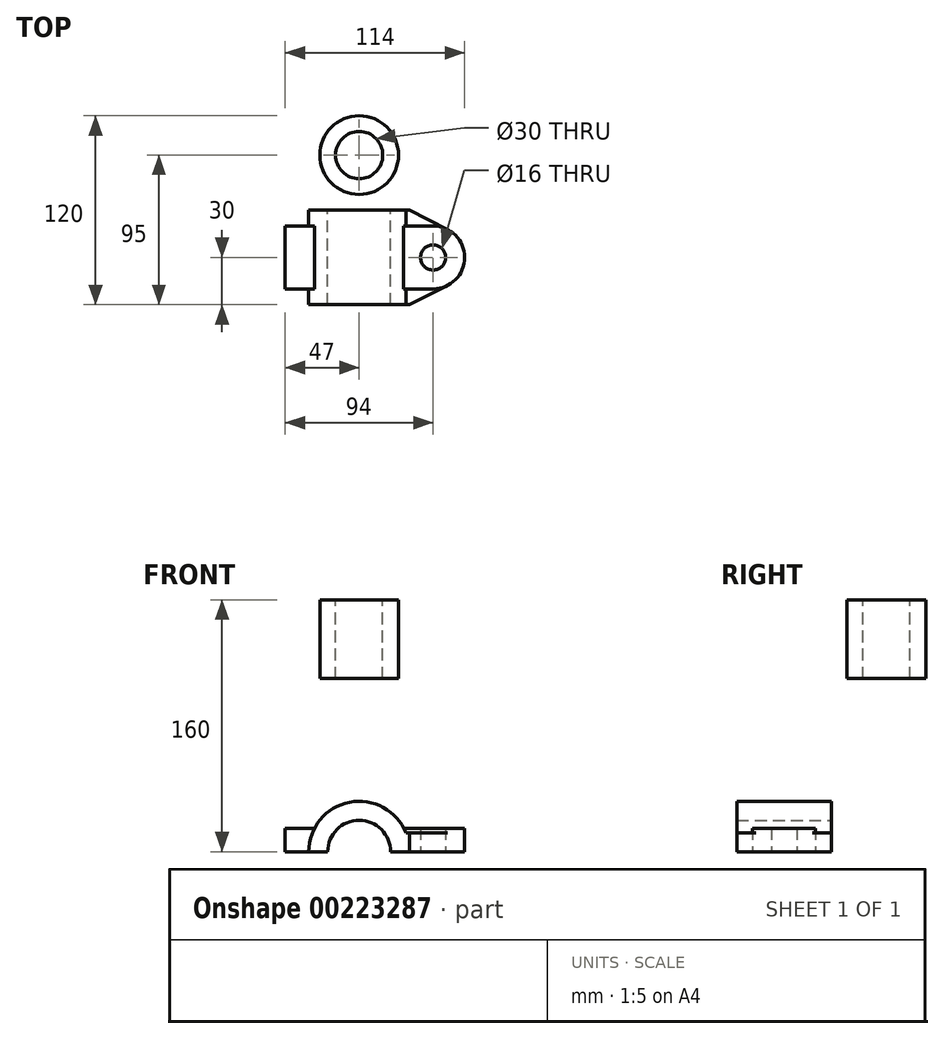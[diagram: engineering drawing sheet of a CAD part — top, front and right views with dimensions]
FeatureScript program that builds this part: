
annotation { "Feature Type Name" : "Feature", "Feature Type Description" : "" }
export const myFeature = defineFeature(function(context is Context, id is Id, definition is map)
    precondition{}
    {
        {
            var Q0;
            Q0=qCreatedBy(makeId("Front.planeOp"),FACE);
            var sketch = newSketch(context, id + "F0", { "sketchPlane" : qUnion([Q0])});
            skArc(sketch, "E0", {"start": v(32, 0) * mm, "mid": v(0, 32) * mm, "end": v(-32, 0) * mm});
            skArc(sketch, "E1", {"start": v(20, 0) * mm, "mid": v(0, 20) * mm, "end": v(-20, 0) * mm});
            skLineSegment(sketch, "E2", {"start": v(-47, 0) * mm, "end": v(47, 0) * mm});
            skLineSegment(sketch, "E3", {"start": v(47, 0) * mm, "end": v(47, 15) * mm});
            skLineSegment(sketch, "E4", {"start": v(47, 15) * mm, "end": v(28.27, 15) * mm});
            skLineSegment(sketch, "E5", {"start": v(-47, 15) * mm, "end": v(-47, 0) * mm});
            skLineSegment(sketch, "E6", {"start": v(0, 67.2) * mm, "end": v(0, -78.93) * mm, "construction": true});
            skLineSegment(sketch, "E7.trimOffspring", {"start": v(-28.27, 15) * mm, "end": v(-47, 15) * mm});
            skSolve(sketch);
        }
        {
            var Q0;
            {var subQ0=sQuery(id+"F0.wireOp",EDGE,"E1");Q0=makeQuery(id+"F0.imprint","IMPRINT",FACE,{"disambiguationData":[TD([[makeQuery(id+"F0.imprint","IMPRINT",EDGE,{"derivedFrom":subQ0}),-1.0]])]});}
            extrude(context, id + "F1", {"entities" : qUnion([Q0]), "endBound" : BoundingType.SYMMETRIC, "depth" : 60 * mm});
        }
        {
            var Q0;
            {var subQ4=sQuery(id+"F0.wireOp",EDGE,"E5");Q0=makeQuery(id+"F0.imprint","IMPRINT",FACE,{"disambiguationData":[TD([[makeQuery(id+"F0.imprint","IMPRINT",EDGE,{"derivedFrom":subQ4}),1.0]])]});}
            var Q1;
            {var subQ4=sQuery(id+"F0.wireOp",EDGE,"E3");Q1=makeQuery(id+"F0.imprint","IMPRINT",FACE,{"disambiguationData":[TD([[makeQuery(id+"F0.imprint","IMPRINT",EDGE,{"derivedFrom":subQ4}),1.0]])]});}
            extrude(context, id + "F2", {"entities" : qUnion([Q0, Q1]), "operationType" : NewBodyOperationType.ADD, "endBound" : BoundingType.SYMMETRIC, "depth" : 40 * mm});
        }
        {
            var Q0;
            Q0=qCreatedBy(makeId("Top.planeOp"),FACE);
            var sketch = newSketch(context, id + "F3", { "sketchPlane" : qUnion([Q0])});
            skCircle(sketch, "E8", {"center": v(47, 0) * mm, "radius": 8 * mm});
            skCircle(sketch, "E9", {"center": v(47, 0) * mm, "radius": 20 * mm});
            skLineSegment(sketch, "E10.0", {"start": v(32, -20) * mm, "end": v(28.27, -20) * mm});
            skLineSegment(sketch, "E11.0", {"start": v(32, 20) * mm, "end": v(28.27, 20) * mm});
            skLineSegment(sketch, "E12", {"start": v(32, -30) * mm, "end": v(56.03, -17.85) * mm});
            skLineSegment(sketch, "E13", {"start": v(32, 30) * mm, "end": v(56.03, 17.85) * mm});
            skPoint(sketch, "E14.0.start.orphan", {"position": v(32, 20) * mm});
            skPoint(sketch, "E15.0.end.orphan", {"position": v(32, -20) * mm});
            skLineSegment(sketch, "E16", {"start": v(32, -30) * mm, "end": v(22, -30) * mm});
            skLineSegment(sketch, "E17", {"start": v(22, -30) * mm, "end": v(22, -20) * mm});
            skLineSegment(sketch, "E18", {"start": v(22, -20) * mm, "end": v(47, -20) * mm});
            skLineSegment(sketch, "E19", {"start": v(47, 20) * mm, "end": v(22, 20) * mm});
            skLineSegment(sketch, "E20", {"start": v(22, 20) * mm, "end": v(22, 30) * mm});
            skLineSegment(sketch, "E21", {"start": v(22, 30) * mm, "end": v(32, 30) * mm});
            skSolve(sketch);
        }
        {
            var Q0;
            Q0=makeQuery(id+"F3.imprint","IMPRINT",FACE,{"disambiguationData":[TD([[makeQuery(id+"F3.imprint","IMPRINT",EDGE,{"derivedFrom":sQuery(id+"F3.wireOp",EDGE,"E8")}),-1.0]])]});
            extrude(context, id + "F4", {"entities" : qUnion([Q0]), "operationType" : NewBodyOperationType.ADD, "depth" : 15 * mm});
        }
        {
            var Q0;
            {var subQ4=sQuery(id+"F3.wireOp",EDGE,"E13");Q0=makeQuery(id+"F3.imprint","IMPRINT",FACE,{"disambiguationData":[TD([[makeQuery(id+"F3.imprint","IMPRINT",EDGE,{"derivedFrom":subQ4}),-1.0]])]});}
            var Q1;
            {var subQ1=sQuery(id+"F3.wireOp",EDGE,"E12");Q1=makeQuery(id+"F3.imprint","IMPRINT",FACE,{"disambiguationData":[TD([[makeQuery(id+"F3.imprint","IMPRINT",EDGE,{"derivedFrom":subQ1}),1.0]])]});}
            extrude(context, id + "F5", {"entities" : qUnion([Q0, Q1]), "operationType" : NewBodyOperationType.ADD, "depth" : 12 * mm});
        }
        {
            var Q0;
            Q0=makeQuery(id+"F3.imprint","IMPRINT",FACE,{"disambiguationData":[TD([[makeQuery(id+"F3.imprint","IMPRINT",EDGE,{"derivedFrom":sQuery(id+"F3.wireOp",EDGE,"E8")}),1.0]])]});
            extrude(context, id + "F6", {"entities" : qUnion([Q0]), "operationType" : NewBodyOperationType.REMOVE, "depth" : 25 * mm});
        }
        {
            var Q0;
            Q0=qCreatedBy(makeId("Top.planeOp"),FACE);
            cPlane(context, id + "F7", {"entities" : qUnion([Q0]), "cplaneType" : CPlaneType.OFFSET, "offset" : 160 * mm, "width" : 150 * mm, "height" : 150 * mm});
        }
        {
            var Q0;
            Q0=qCreatedBy(id+"F7.planeOp",FACE);
            var sketch = newSketch(context, id + "F8", { "sketchPlane" : qUnion([Q0])});
            skCircle(sketch, "E22", {"center": v(0, 65) * mm, "radius": 25 * mm});
            skCircle(sketch, "E23", {"center": v(0, 65) * mm, "radius": 15 * mm});
            skLineSegment(sketch, "E24", {"start": v(0, -98.9) * mm, "end": v(0, 161.69) * mm, "construction": true});
            skLineSegment(sketch, "E25", {"start": v(-5, 65) * mm, "end": v(5, 65) * mm});
            skLineSegment(sketch, "E26", {"start": v(5, -46.71) * mm, "end": v(-5, -46.71) * mm});
            skLineSegment(sketch, "E27.0", {"start": v(29.66, -30) * mm, "end": v(-29.66, -30) * mm, "construction": true});
            skSolve(sketch);
        }
        {
            var Q0;
            Q0=makeQuery(id+"F8.imprint","IMPRINT",FACE,{"disambiguationData":[TD([[makeQuery(id+"F8.imprint","IMPRINT",EDGE,{"derivedFrom":sQuery(id+"F8.wireOp",EDGE,"E22")}),1.0]])]});
            extrude(context, id + "F9", {"entities" : qUnion([Q0]), "oppositeDirection" : true, "depth" : 50 * mm});
        }
    });
